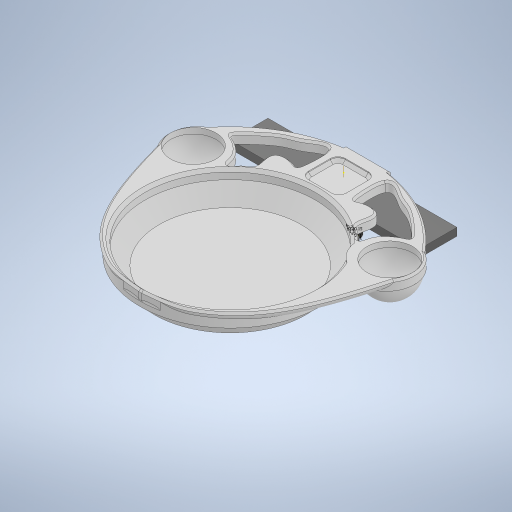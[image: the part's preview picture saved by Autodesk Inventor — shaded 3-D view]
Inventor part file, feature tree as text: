
AUTODESK INVENTOR PART (.ipt)
format: ipt  version: 2024.1 (Build 281209000, 209)  size: 1,652,224 bytes
history: native  units: mm
features: extrude x18, projected_geometry x15, sketch x11, chamfer x11, fillet x9, helix x2, other x2, hole x1, plane x1, thread x1, pattern_circular x1, mirror x1, revolve x1
ambient origin geometry x8: Origin, YZ Plane, XZ Plane, XY Plane, X Axis, Y Axis, Z Axis, Center Point
bodies: Solid1 (feature_tree)
feature tree (74):
  extrude  "Extrusion1"  Depth=40.0mm
  extrude  "Extrusion2"  Depth=20.0mm
  extrude  "Extrusion3"  Depth=45.0mm
  extrude  "Extrusion4"  Depth=10.0mm
  extrude  "Extrusion5"  Depth=10.0mm TaperAngle=0.0deg
  hole  "Hole1"  [1 undecoded]
  plane  "Work Plane1"
  extrude  "Extrusion6"  Depth=10.0mm TaperAngle=0.0deg
  extrude  "Extrusion7"  Depth=2.0mm
  extrude  "Extrusion20"  Depth=10.0mm TaperAngle=0.0deg
  sketch  "Sketch24"  dims[d19=12.0mm]
  helix  "Coil1"  [1 undecoded]
  helix  "Coil2"  [1 undecoded]
  chamfer  "Chamfer8"  Distance=30.0mm
  chamfer  "Chamfer9"  Distance=2.0mm Angle=45.0deg
  thread  "Thread1"  [1 undecoded]
  fillet  "Fillet1"  [1 undecoded]
  chamfer  "Chamfer1"  Distance=60.0mm Angle=360.0deg
  extrude  "Extrusion8"  Depth=10.0mm
  pattern_circular  "Circular Pattern1"  Count=18  [1 undecoded]
  fillet  "Fillet2"  Radius=90.0mm
  extrude  "Extrusion9"  Depth=10.0mm
  sketch  "Sketch13"  dims[d2=100.0mm d3=20.0mm]
  extrude  "Extrusion18"  Depth=10.0mm
  extrude  "Extrusion19"  Depth=10.0mm
  chamfer  "Chamfer5"  Distance=100.0mm
  chamfer  "Chamfer10"  Distance=50.0mm
  fillet  "Fillet17"  Radius=50.0mm
  extrude  "Extrusion11"  Depth=10.0mm TaperAngle=0.0deg
  chamfer  "Chamfer2"  Distance=3.0mm
  fillet  "Fillet8"  Radius=50.0mm
  chamfer  "Chamfer3"  Distance=2.0mm Angle=45.0deg
  fillet  "Fillet9"  Radius=10.0mm
  chamfer  "Chamfer11"  Distance=2.0mm Angle=45.0deg
  extrude  "Extrusion14"  Depth=10.0mm
  mirror  "Mirror1"
  extrude  "Extrusion15"  Depth=10.0mm
  revolve  "Revolution1"  [1 undecoded]
  fillet  "Fillet11"  Radius=13.0mm
  chamfer  "Chamfer12"  Distance=138.0mm
  extrude  "Extrusion16"  TaperAngle=0.0deg  [1 undecoded]
  extrude  "Extrusion17"  Depth=10.0mm
  fillet  "Fillet13"  Radius=20.057674mm
  fillet  "Fillet14"  Radius=25.0mm
  chamfer  "Chamfer4"  Distance=4.0mm
  fillet  "Fillet16"  Radius=8.0mm
  chamfer  "Chamfer13"  Distance=20.0mm
  extrude  "Extrusion21"  Depth=10.0mm TaperAngle=0.0deg
  other  "clamp"
  projected_geometry  "Projected Loop1"
  projected_geometry  "Projected Loop2"
  projected_geometry  "Projected Loop3"
  other  "screw"
  projected_geometry  "Projected Loop5"
  sketch  "Sketch12"  dims[d0=200.0mm d1=40.0mm]
  projected_geometry  "Projected Loop6"
  projected_geometry  "Projected Loop7"
  sketch  "Sketch17"  dims[d4=8.2mm d5=0.0mm d6=45.0mm]
  projected_geometry  "Projected Loop12"
  sketch  "Sketch20"  dims[d7=22.5mm d8=10.0mm]
  projected_geometry  "Projected Loop13"
  sketch  "Sketch21"  dims[d9=10.0mm d10=10.0mm d11=0.0mm]
  projected_geometry  "Projected Loop15"
  projected_geometry  "Projected Loop16"
  sketch  "Sketch22"  dims[d12=10.0mm d13=0.0mm d14=20.0mm d15=0.0mm]
  sketch  "Sketch23"  dims[d16=39.0mm d17=10.0mm d18=0.0mm]
  projected_geometry  "Projected Loop18"
  projected_geometry  "Projected Loop19"
  sketch  "Sketch25"  dims[d20=12.0mm d21=24.0mm d22=3.023mm d23=2.0mm d24=90.0deg d25=32.3mm d26=0.0mm d27=15.0mm]
  projected_geometry  "Projected Loop20"
  sketch  "Sketch26"  dims[d28=30.0mm d29=10.0mm d30=0.0mm d32=12.0mm d33=27.0mm d34=0.0mm d35=30.0mm d36=0.0mm]
  sketch  "Sketch27"  dims[d37=2.0mm d38=2.0mm d39=2.0mm d40=45.0deg d41=8.5mm d42=0.0mm d43=0.0mm d44=60.0mm d45=360.0deg d47=3.0mm d48=180.0mm d49=90.0mm d51=60.0mm d52=35.0mm d53=100.0mm d54=100.0mm d55=50.0mm d56=50.0mm d57=10.0mm d58=0.0mm d59=3.0mm d65=50.0mm d66=0.0mm d71=2.0mm d72=2.0mm d73=45.0deg d74=10.0mm d75=5.0mm d76=2.0mm d77=45.0deg d78=27.0mm d87=13.0mm d88=13.0mm d89=13.0mm d90=138.0mm d92=0.0mm d93=0.0mm d97=20.057674mm d98=20.057674mm d99=25.0mm d100=4.0mm d101=0.0mm d102=8.0mm d104=20.0mm d105=0.0mm d106=3.0mm d107=0.0mm d108=24.0mm d109=25.0mm d111=2.0mm d112=2.0mm d113=45.0deg d114=14.0mm d115=40.115347mm d116=1.7mm d119=15.0mm d120=0.0mm d121=5.0mm d122=0.0mm d123=15.0mm d124=2.0mm d125=45.0deg d129=6.0mm d133=2.0mm d135=1.0mm d136=2.4mm d137=20.0mm d138=10.0mm d139=0.0mm d140=90.0deg d141=90.0deg d142=0.0mm d143=0.0mm d144=2.5mm d145=25.0mm d146=10.0mm d147=0.0mm d148=90.0deg d149=90.0deg d150=0.0mm d151=0.0mm d152=0.15mm d156=0.2mm d157=0.2mm d158=1.5mm d159=1.5mm d160=5.0mm d161=0.0mm d162=0.5mm d163=2.0mm d164=45.0deg d165=0.5mm d166=2.0mm d167=45.0deg d168=3.0mm d169=2.0mm d170=45.0deg d171=20.0mm d172=3.0mm d173=2.0mm d174=45.0deg d175=1.0mm d176=4.0mm d177=1.5mm d178=6.0mm d179=360.0deg d180=3.0mm d181=2.0mm d182=45.0deg d183=3.0mm d184=2.0mm d185=45.0deg d186=2.0mm d187=10.0mm d188=0.0mm]
  projected_geometry  "Projected Loop21"
  projected_geometry  "Projected Loop22"
note: 8 required parameter values undecoded (feature->parameter linkage not recoverable at this tier; creation-order binding heuristic only, values carry confidence <= 0.55)